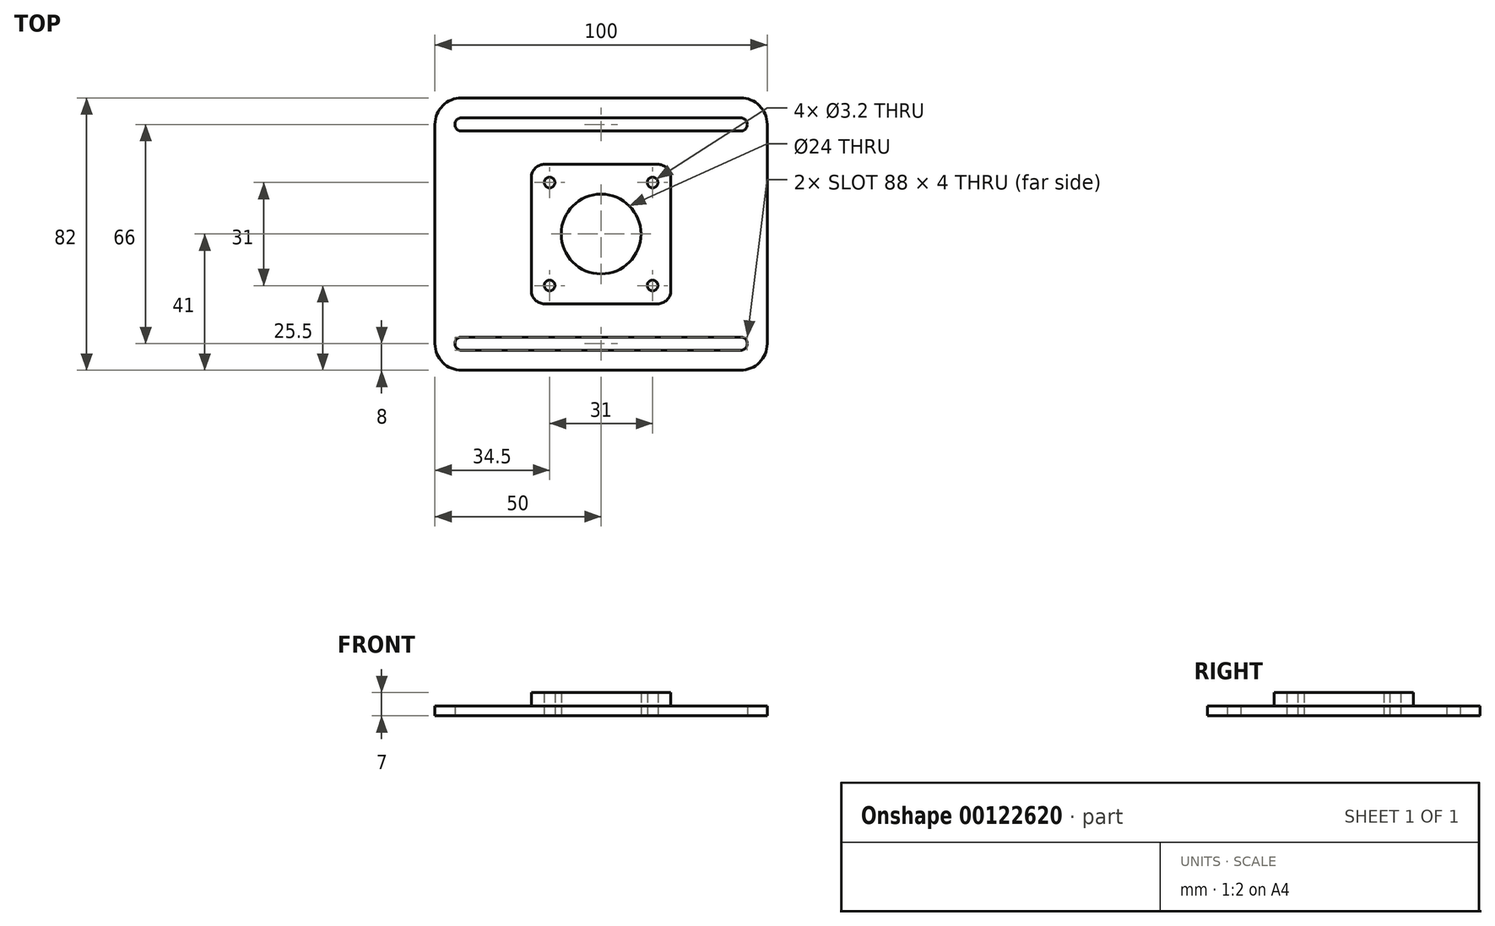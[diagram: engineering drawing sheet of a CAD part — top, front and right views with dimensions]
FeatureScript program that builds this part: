
annotation { "Feature Type Name" : "Feature", "Feature Type Description" : "" }
export const myFeature = defineFeature(function(context is Context, id is Id, definition is map)
    precondition{}
    {
        {
            var Q0;
            Q0=qCreatedBy(makeId("Top.planeOp"),FACE);
            var sketch = newSketch(context, id + "F0", { "sketchPlane" : qUnion([Q0])});
            skCircle(sketch, "E0", {"center": v(0, 0) * mm, "radius": 12 * mm});
            skLineSegment(sketch, "E1.bottom", {"start": v(15.5, 15.5) * mm, "end": v(-15.5, 15.5) * mm, "construction": true});
            skLineSegment(sketch, "E1.top", {"start": v(15.5, -15.5) * mm, "end": v(-15.5, -15.5) * mm, "construction": true});
            skLineSegment(sketch, "E1.left", {"start": v(15.5, 15.5) * mm, "end": v(15.5, -15.5) * mm, "construction": true});
            skLineSegment(sketch, "E1.right", {"start": v(-15.5, 15.5) * mm, "end": v(-15.5, -15.5) * mm, "construction": true});
            skCircle(sketch, "E2", {"center": v(-15.5, 15.5) * mm, "radius": 1.6 * mm});
            skCircle(sketch, "E3", {"center": v(15.5, 15.5) * mm, "radius": 1.6 * mm});
            skCircle(sketch, "E4", {"center": v(15.5, -15.5) * mm, "radius": 1.6 * mm});
            skCircle(sketch, "E5", {"center": v(-15.5, -15.5) * mm, "radius": 1.6 * mm});
            skLineSegment(sketch, "E6.bottom", {"start": v(42, 41) * mm, "end": v(-42, 41) * mm});
            skLineSegment(sketch, "E6.top", {"start": v(42, -41) * mm, "end": v(-42, -41) * mm});
            skLineSegment(sketch, "E6.left", {"start": v(50, 33) * mm, "end": v(50, -33) * mm});
            skLineSegment(sketch, "E6.right", {"start": v(-50, 33) * mm, "end": v(-50, -33) * mm});
            skLineSegment(sketch, "E7", {"start": v(-42, -33) * mm, "end": v(42, -33) * mm});
            skLineSegment(sketch, "E8", {"start": v(-42, 33) * mm, "end": v(42, 33) * mm});
            skPoint(sketch, "E9", {"position": v(0, -33) * mm});
            skPoint(sketch, "E10", {"position": v(0, 33) * mm});
            skArc(sketch, "E11.0.startCap", {"start": v(-42, 31) * mm, "mid": v(-44, 33) * mm, "end": v(-42, 35) * mm});
            skArc(sketch, "E11.0.endCap", {"start": v(42, 35) * mm, "mid": v(44, 33) * mm, "end": v(42, 31) * mm});
            skLineSegment(sketch, "E11.0.left", {"start": v(-42, 35) * mm, "end": v(42, 35) * mm});
            skLineSegment(sketch, "E11.0.right", {"start": v(-42, 31) * mm, "end": v(42, 31) * mm});
            skArc(sketch, "E12.0.startCap", {"start": v(-42, -35) * mm, "mid": v(-44, -33) * mm, "end": v(-42, -31) * mm});
            skArc(sketch, "E12.0.endCap", {"start": v(42, -31) * mm, "mid": v(44, -33) * mm, "end": v(42, -35) * mm});
            skLineSegment(sketch, "E12.0.left", {"start": v(-42, -31) * mm, "end": v(42, -31) * mm});
            skLineSegment(sketch, "E12.0.right", {"start": v(-42, -35) * mm, "end": v(42, -35) * mm});
            skPoint(sketch, "E13.visualSharp", {"position": v(-50, 41) * mm});
            skArc(sketch, "E13.filletArc", {"start": v(-42, 41) * mm, "mid": v(-47.66, 38.66) * mm, "end": v(-50, 33) * mm});
            skPoint(sketch, "E14.visualSharp", {"position": v(50, 41) * mm});
            skArc(sketch, "E14.filletArc", {"start": v(50, 33) * mm, "mid": v(47.66, 38.66) * mm, "end": v(42, 41) * mm});
            skPoint(sketch, "E15.visualSharp", {"position": v(50, -41) * mm});
            skArc(sketch, "E15.filletArc", {"start": v(42, -41) * mm, "mid": v(47.66, -38.66) * mm, "end": v(50, -33) * mm});
            skPoint(sketch, "E16.visualSharp", {"position": v(-50, -41) * mm});
            skArc(sketch, "E16.filletArc", {"start": v(-50, -33) * mm, "mid": v(-47.66, -38.66) * mm, "end": v(-42, -41) * mm});
            skSolve(sketch);
        }
        {
            var Q0;
            Q0=makeQuery(id+"F0.imprint","IMPRINT",FACE,{"disambiguationData":[TD([[makeQuery(id+"F0.imprint","IMPRINT",EDGE,{"derivedFrom":sQuery(id+"F0.wireOp",EDGE,"E0")}),-1.0]])]});
            extrude(context, id + "F1", {"entities" : qUnion([Q0]), "depth" : 3 * mm});
        }
        {
            var Q0;
            Q0=makeQuery(id+"F1.opExtrude","CAP_FACE",FACE,{"disambiguationData":[OSD([sQuery(id+"F0.wireOp",EDGE,"E0"),sQuery(id+"F0.wireOp",EDGE,"E2"),sQuery(id+"F0.wireOp",EDGE,"E3"),sQuery(id+"F0.wireOp",EDGE,"E4"),sQuery(id+"F0.wireOp",EDGE,"E5"),sQuery(id+"F0.wireOp",EDGE,"E6.bottom"),sQuery(id+"F0.wireOp",EDGE,"E6.top"),sQuery(id+"F0.wireOp",EDGE,"E6.left"),sQuery(id+"F0.wireOp",EDGE,"E6.right"),sQuery(id+"F0.wireOp",EDGE,"E11.0.startCap"),sQuery(id+"F0.wireOp",EDGE,"E11.0.endCap"),sQuery(id+"F0.wireOp",EDGE,"E11.0.left"),sQuery(id+"F0.wireOp",EDGE,"E11.0.right"),sQuery(id+"F0.wireOp",EDGE,"E12.0.startCap"),sQuery(id+"F0.wireOp",EDGE,"E12.0.endCap"),sQuery(id+"F0.wireOp",EDGE,"E12.0.left"),sQuery(id+"F0.wireOp",EDGE,"E12.0.right"),sQuery(id+"F0.wireOp",EDGE,"E13.filletArc"),sQuery(id+"F0.wireOp",EDGE,"E14.filletArc"),sQuery(id+"F0.wireOp",EDGE,"E15.filletArc"),sQuery(id+"F0.wireOp",EDGE,"E16.filletArc")])],"isStart":false});
            var sketch = newSketch(context, id + "F2", { "sketchPlane" : qUnion([Q0])});
            skLineSegment(sketch, "E17.bottom", {"start": v(17, 21) * mm, "end": v(-17, 21) * mm});
            skLineSegment(sketch, "E17.top", {"start": v(17, -21) * mm, "end": v(-17, -21) * mm});
            skLineSegment(sketch, "E17.left", {"start": v(21, 17) * mm, "end": v(21, -17) * mm});
            skLineSegment(sketch, "E17.right", {"start": v(-21, 17) * mm, "end": v(-21, -17) * mm});
            skPoint(sketch, "E17.middle", {"position": v(0, 0) * mm});
            skPoint(sketch, "E18.visualSharp", {"position": v(-21, 21) * mm});
            skArc(sketch, "E18.filletArc", {"start": v(-17, 21) * mm, "mid": v(-19.83, 19.83) * mm, "end": v(-21, 17) * mm});
            skPoint(sketch, "E19.visualSharp", {"position": v(21, 21) * mm});
            skArc(sketch, "E19.filletArc", {"start": v(21, 17) * mm, "mid": v(19.83, 19.83) * mm, "end": v(17, 21) * mm});
            skPoint(sketch, "E20.visualSharp", {"position": v(21, -21) * mm});
            skArc(sketch, "E20.filletArc", {"start": v(17, -21) * mm, "mid": v(19.83, -19.83) * mm, "end": v(21, -17) * mm});
            skPoint(sketch, "E21.visualSharp", {"position": v(-21, -21) * mm});
            skArc(sketch, "E21.filletArc", {"start": v(-21, -17) * mm, "mid": v(-19.83, -19.83) * mm, "end": v(-17, -21) * mm});
            skSolve(sketch);
        }
        {
            var Q0;
            Q0=makeQuery(id+"F2.imprint","IMPRINT",FACE,{"disambiguationData":[TD([[makeQuery(id+"F2.imprint","IMPRINT",EDGE,{"derivedFrom":sQuery(id+"F2.wireOp",EDGE,"E17.bottom")}),1.0]])]});
            extrude(context, id + "F3", {"entities" : qUnion([Q0]), "operationType" : NewBodyOperationType.ADD, "depth" : 4 * mm});
        }
    });
